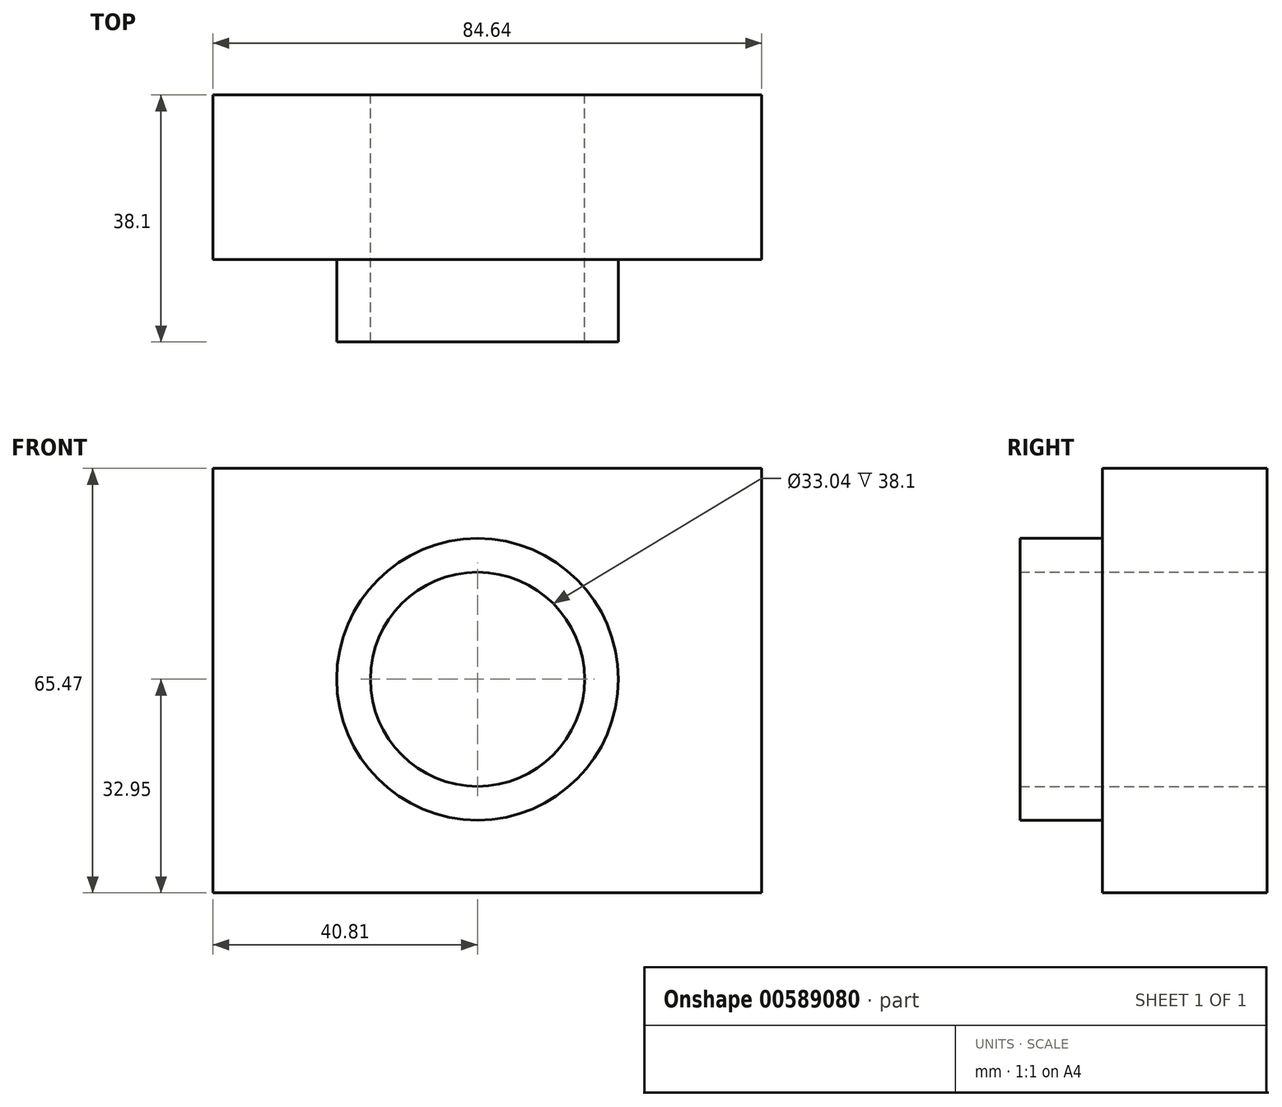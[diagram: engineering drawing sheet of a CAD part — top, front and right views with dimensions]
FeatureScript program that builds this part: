
annotation { "Feature Type Name" : "Feature", "Feature Type Description" : "" }
export const myFeature = defineFeature(function(context is Context, id is Id, definition is map)
    precondition{}
    {
        {
            var Q0;
            Q0=qCreatedBy(makeId("Front.planeOp"),FACE);
            var sketch = newSketch(context, id + "F0", { "sketchPlane" : qUnion([Q0])});
            skLineSegment(sketch, "E0", {"start": v(-40.81, 32.52) * mm, "end": v(43.83, 32.52) * mm});
            skLineSegment(sketch, "E1", {"start": v(43.83, 32.52) * mm, "end": v(43.83, -32.95) * mm});
            skLineSegment(sketch, "E2", {"start": v(43.83, -32.95) * mm, "end": v(-40.81, -32.95) * mm});
            skLineSegment(sketch, "E3", {"start": v(-40.81, -32.95) * mm, "end": v(-40.81, 32.52) * mm});
            skCircle(sketch, "E4", {"center": v(0, 0) * mm, "radius": 16.52 * mm});
            skCircle(sketch, "E5", {"center": v(0, 0) * mm, "radius": 21.72 * mm});
            skSolve(sketch);
        }
        {
            var Q0;
            Q0=makeQuery(id+"F0.imprint","IMPRINT",FACE,{"disambiguationData":[TD([[makeQuery(id+"F0.imprint","IMPRINT",EDGE,{"derivedFrom":sQuery(id+"F0.wireOp",EDGE,"E4")}),-1.0]])]});
            extrude(context, id + "F1", {"entities" : qUnion([Q0]), "depth" : 38.1 * mm, "offsetDistance" : 25.4 * mm});
        }
        {
            var Q0;
            Q0=makeQuery(id+"F0.imprint","IMPRINT",FACE,{"disambiguationData":[TD([[makeQuery(id+"F0.imprint","IMPRINT",EDGE,{"derivedFrom":sQuery(id+"F0.wireOp",EDGE,"E0")}),-1.0]])]});
            extrude(context, id + "F2", {"entities" : qUnion([Q0]), "operationType" : NewBodyOperationType.ADD, "depth" : 25.4 * mm, "offsetDistance" : 25.4 * mm});
        }
    });
